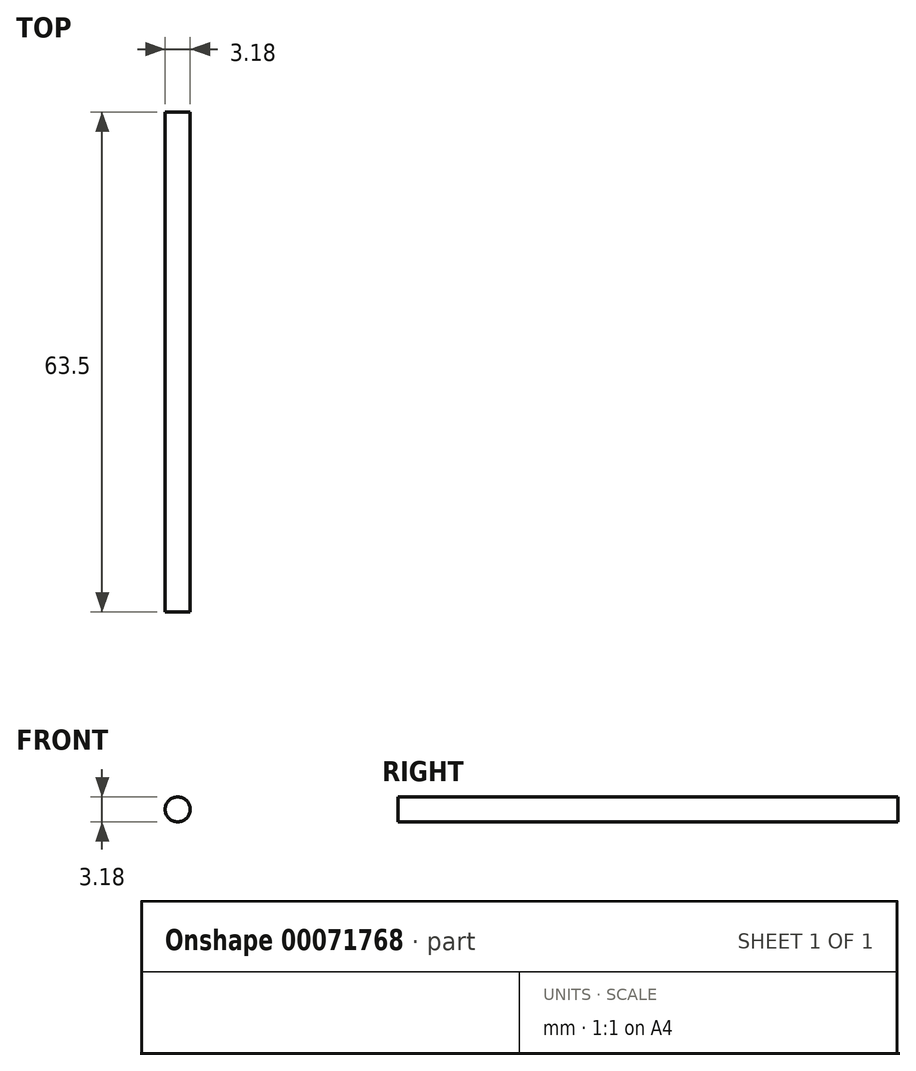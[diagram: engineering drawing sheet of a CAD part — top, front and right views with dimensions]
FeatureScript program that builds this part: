
annotation { "Feature Type Name" : "Feature", "Feature Type Description" : "" }
export const myFeature = defineFeature(function(context is Context, id is Id, definition is map)
    precondition{}
    {
        {
            var Q0;
            Q0=qCreatedBy(makeId("Front.planeOp"),FACE);
            var sketch = newSketch(context, id + "F0", { "sketchPlane" : qUnion([Q0])});
            skCircle(sketch, "E0", {"center": v(0, 0) * mm, "radius": 1.59 * mm});
            skSolve(sketch);
        }
        {
            var Q0;
            Q0=makeQuery(id+"F0.imprint","IMPRINT",FACE,{"disambiguationData":[TD([[makeQuery(id+"F0.imprint","IMPRINT",EDGE,{"derivedFrom":sQuery(id+"F0.wireOp",EDGE,"E0")}),1.0]])]});
            extrude(context, id + "F1", {"entities" : qUnion([Q0]), "depth" : 63.5 * mm});
        }
    });
